# Revit family: Grohe_PlumbingFixtures_RapidSL_WallBrackets_3855800M_a
name_source: partatom
category: Plumbing Fixtures
revit_build: Autodesk Revit 2016 (Build: 20150714_1515(x64)
units: mm (PartAtom-declared; Revit-internal decimal feet)

## family parameters
Cut with Voids When Loaded = No
Host = Face
OmniClass Number = 23.45.05.00
OmniClass Title = Sanitary Equipment
Part Type = Normal
Room Calculation Point = No
Round Connector Dimension = Use Diameter
Shared = No

## types (1)
- 3855800M
    ADACompliant = No
    Assembly Code = C1030
    AssetType = Fixed
    BIMObjectName = Grohe_PlumbingFixtures_RapidSL_WallBrackets_3855800M
    ClassificationName = Uniclass2015
    ColdWaterConnectionDiameter = 10 mm  [stored 0.0328084 ft]
    Color = Silver
    Cost = 0 $
    Default Elevation = 0 mm  [stored 0 ft]
    Description = for on-the-wall installations
for fixing the elements at the brick-wall 
or in front of the studded wall
steady vertical adjustment from 
130 - 230 mm
cladding for single or series installation
fixing material
2 pieces
    DocumentationInstallationGuide = https://specifi.bimstore.co.uk
    DocumentationLiterature = https://specifi.bimstore.co.uk
    DocumentationTechnical = https://specifi.bimstore.co.uk
    DurationUnit = Years
    Ecojoy = No
    ExpectedLife = 0
    Features = for on-the-wall installations
for fixing the elements at the brick-wall 
or in front of the studded wall
steady vertical adjustment from 
130 - 230 mm
cladding for single or series installation
fixing material
2 pieces
    Finish = Stainless steel
    HotWaterConnectionDiameter = 10 mm  [stored 0.0328084 ft]
    IfcExportAs = IfcPipeFitting
    IfcExportType = IfcPipeFittingType
    Keynote = N13
    LowEmittingMaterial = No
    Manufacturer = Grohe
    ManufacturerName = Grohe
    MasterformatNumber = 01 52 19
    MasterformatTitle = Sanitary Facilities
    Model = Rapid SL wall brackets
    ModelNumber = 3855800M
    ModelReference = Rapid SL wall brackets
    NBSObjectName = Grohe - n/a
    NominalDepth = 0 mm  [stored 0 ft]
    NominalHeight = 0 mm  [stored 0 ft]
    NominalLength = 230 mm
    ProductDocumentationLink = https://www.grohe.com
    ProductPageURL = https://www.grohe.com
    ProductionYear = 2018
    Type Comments = 3855800M
    TypeName = Rapid SL wall brackets
    URL = https://www.grohe.co.uk
    WarrantyDurationLabor = 0
    WarrantyDurationParts = 0
    WarrantyDurationUnit = Years
    _BSBibleVersion = 15
    _BimSpecGuid = 0
    _CurrentRevision = 1
    _DistributedBy = www.bimstore.co.uk

note: [stored X ft] marks values corroborated as IEEE doubles in the binary element streams (Revit-internal decimal feet)

## geometry (parser evidence)
native form markers: Blend x4, Sweep x2
no freeform markers — native parametric forms only
